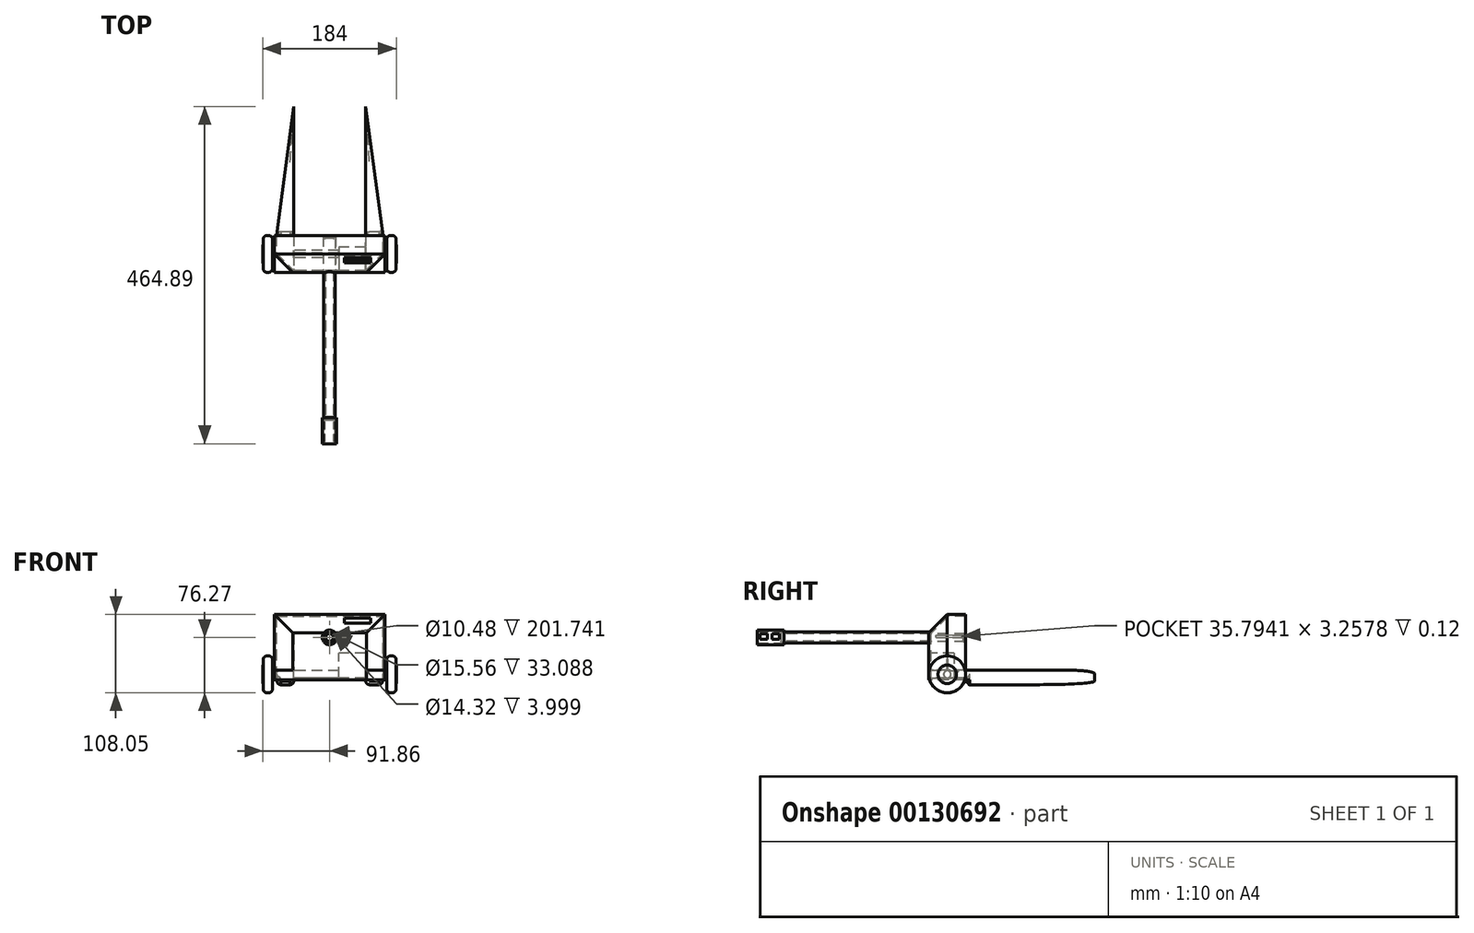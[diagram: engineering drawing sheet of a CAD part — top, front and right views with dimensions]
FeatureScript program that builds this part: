
annotation { "Feature Type Name" : "Feature", "Feature Type Description" : "" }
export const myFeature = defineFeature(function(context is Context, id is Id, definition is map)
    precondition{}
    {
        {
            var Q0;
            Q0=qCreatedBy(makeId("Front.planeOp"),FACE);
            var sketch = newSketch(context, id + "F0", { "sketchPlane" : qUnion([Q0])});
            skCircle(sketch, "E0", {"center": v(0, 0) * mm, "radius": 7.78 * mm});
            skCircle(sketch, "E1", {"center": v(0, 0) * mm, "radius": 10.04 * mm});
            skSolve(sketch);
        }
        {
            var Q0;
            Q0=makeQuery(id+"F0.imprint","IMPRINT",FACE,{"disambiguationData":[TD([[makeQuery(id+"F0.imprint","IMPRINT",EDGE,{"derivedFrom":sQuery(id+"F0.wireOp",EDGE,"E0")}),-1.0]])]});
            extrude(context, id + "F1", {"entities" : qUnion([Q0]), "depth" : 33.1 * mm, "hasSecondDirection" : true, "secondDirectionOppositeDirection" : true, "secondDirectionDepth" : 3.3 * mm});
        }
        {
            var Q0;
            Q0=makeQuery(id+"F0.imprint","IMPRINT",FACE,{"disambiguationData":[TD([[makeQuery(id+"F0.imprint","IMPRINT",EDGE,{"derivedFrom":sQuery(id+"F0.wireOp",EDGE,"E0")}),1.0]])]});
            extrude(context, id + "F2", {"entities" : qUnion([Q0]), "operationType" : NewBodyOperationType.ADD, "oppositeDirection" : true, "depth" : 203.2 * mm});
        }
        {
            var Q0;
            Q0=makeQuery(id+"F2.opExtrude","CAP_FACE",FACE,{"disambiguationData":[OSD([sQuery(id+"F0.wireOp",EDGE,"E0")])],"isStart":false});
            var sketch = newSketch(context, id + "F3", { "sketchPlane" : qUnion([Q0])});
            skLineSegment(sketch, "E2.bottom", {"start": v(-76.37, 31.78) * mm, "end": v(76.03, 31.78) * mm});
            skLineSegment(sketch, "E2.top", {"start": v(-76.37, -58.3) * mm, "end": v(76.03, -58.3) * mm});
            skLineSegment(sketch, "E2.left", {"start": v(-76.37, 31.78) * mm, "end": v(-76.37, -58.3) * mm});
            skLineSegment(sketch, "E2.right", {"start": v(76.03, 31.78) * mm, "end": v(76.03, -58.3) * mm});
            skSolve(sketch);
        }
        {
            var Q0;
            Q0 = qSketchRegion(id + "F3", true);
            extrude(context, id + "F4", {"entities" : qUnion([Q0]), "operationType" : NewBodyOperationType.ADD, "depth" : 50.8 * mm});
        }
        {
            var Q0;
            Q0=makeQuery(id+"F4.opExtrude","CAP_EDGE",EDGE,{"disambiguationData":[OSD([sQuery(id+"F3.wireOp",EDGE,"E2.right")])],"isStart":true});
            var Q1;
            Q1=makeQuery(id+"F4.opExtrude","CAP_EDGE",EDGE,{"disambiguationData":[OSD([sQuery(id+"F3.wireOp",EDGE,"E2.left")])],"isStart":true});
            var Q2;
            Q2=makeQuery(id+"F4.opExtrude","CAP_EDGE",EDGE,{"disambiguationData":[OSD([sQuery(id+"F3.wireOp",EDGE,"E2.bottom")])],"isStart":true});
            chamfer(context, id + "F5", {"entities" : qUnion([Q0, Q1, Q2]), "width" : 25.4 * mm, "tangentPropagation" : true});
        }
        {
            var Q0;
            Q0=makeQuery(id+"F4.opExtrude","CAP_FACE",FACE,{"disambiguationData":[OSD([sQuery(id+"F3.wireOp",EDGE,"E2.bottom"),sQuery(id+"F3.wireOp",EDGE,"E2.top"),sQuery(id+"F3.wireOp",EDGE,"E2.left"),sQuery(id+"F3.wireOp",EDGE,"E2.right")])],"isStart":false});
            shell(context, id + "F6", {"entities" : qUnion([Q0]), "thickness" : 2.54 * mm});
        }
        {
            var Q0;
            Q0=qCreatedBy(makeId("Front.planeOp"),FACE);
            var sketch = newSketch(context, id + "F7", { "sketchPlane" : qUnion([Q0])});
            skLineSegment(sketch, "E3.bottom", {"start": v(20.34, 26.67) * mm, "end": v(56.85, 26.67) * mm});
            skLineSegment(sketch, "E3.top", {"start": v(20.34, 19.54) * mm, "end": v(56.85, 19.54) * mm});
            skLineSegment(sketch, "E3.left", {"start": v(20.34, 26.67) * mm, "end": v(20.34, 19.54) * mm});
            skLineSegment(sketch, "E3.right", {"start": v(56.85, 26.67) * mm, "end": v(56.85, 19.54) * mm});
            skSolve(sketch);
        }
        {
            var Q0;
            Q0 = qSketchRegion(id + "F7", true);
            extrude(context, id + "F8", {"entities" : qUnion([Q0]), "operationType" : NewBodyOperationType.REMOVE, "oppositeDirection" : true, "depth" : 279.63 * mm});
        }
        {
            var Q0;
            Q0=qCreatedBy(makeId("Right.planeOp"),FACE);
            var sketch = newSketch(context, id + "F9", { "sketchPlane" : qUnion([Q0])});
            skLineSegment(sketch, "E4.bottom", {"start": v(-29.7, 5.03) * mm, "end": v(-19.53, 5.03) * mm});
            skLineSegment(sketch, "E4.top", {"start": v(-29.7, -2.59) * mm, "end": v(-19.53, -2.59) * mm});
            skLineSegment(sketch, "E4.left", {"start": v(-29.7, 5.03) * mm, "end": v(-29.7, -2.59) * mm});
            skLineSegment(sketch, "E4.right", {"start": v(-19.53, 5.03) * mm, "end": v(-19.53, -2.59) * mm});
            skLineSegment(sketch, "E5.bottom", {"start": v(-12.8, 5.03) * mm, "end": v(-2.65, 5.03) * mm});
            skLineSegment(sketch, "E5.top", {"start": v(-12.8, -2.59) * mm, "end": v(-2.65, -2.59) * mm});
            skLineSegment(sketch, "E5.left", {"start": v(-12.8, 5.03) * mm, "end": v(-12.8, -2.59) * mm});
            skLineSegment(sketch, "E5.right", {"start": v(-2.65, 5.03) * mm, "end": v(-2.65, -2.59) * mm});
            skSolve(sketch);
        }
        {
            var Q0;
            Q0 = qSketchRegion(id + "F9", true);
            extrude(context, id + "F10", {"entities" : qUnion([Q0]), "operationType" : NewBodyOperationType.REMOVE, "oppositeDirection" : true, "depth" : 25.4 * mm, "hasSecondDirection" : true, "secondDirectionOppositeDirection" : false, "secondDirectionDepth" : 29.94 * mm});
        }
        {
            var Q0;
            Q0=makeQuery(id+"F0.imprint","IMPRINT",FACE,{"disambiguationData":[TD([[makeQuery(id+"F0.imprint","IMPRINT",EDGE,{"derivedFrom":sQuery(id+"F0.wireOp",EDGE,"E0")}),1.0]])]});
            var sketch = newSketch(context, id + "F11", { "sketchPlane" : qUnion([Q0])});
            skCircle(sketch, "E6", {"center": v(0, 0) * mm, "radius": 7.16 * mm});
            skSolve(sketch);
        }
        {
            var Q0;
            Q0 = qSketchRegion(id + "F11", true);
            extrude(context, id + "F12", {"entities" : qUnion([Q0]), "operationType" : NewBodyOperationType.REMOVE, "oppositeDirection" : true, "depth" : 4 * mm});
        }
        {
            var Q0;
            Q0=makeQuery(id+"F4.opExtrude","SWEPT_FACE",FACE,{"disambiguationData":[OSD([sQuery(id+"F3.wireOp",EDGE,"E2.left")])]});
            var sketch = newSketch(context, id + "F13", { "sketchPlane" : qUnion([Q0])});
            skLineSegment(sketch, "E7.bottom", {"start": v(254, -58.3) * mm, "end": v(203.24, -58.3) * mm});
            skLineSegment(sketch, "E7.top", {"start": v(254, -45) * mm, "end": v(203.24, -45) * mm});
            skLineSegment(sketch, "E7.left", {"start": v(254, -58.3) * mm, "end": v(254, -45) * mm});
            skLineSegment(sketch, "E7.right", {"start": v(203.24, -58.3) * mm, "end": v(203.24, -45) * mm});
            skSolve(sketch);
        }
        {
            var Q0;
            Q0 = qSketchRegion(id + "F13", true);
            extrude(context, id + "F14", {"entities" : qUnion([Q0]), "operationType" : NewBodyOperationType.ADD, "oppositeDirection" : true, "depth" : 26.42 * mm});
        }
        {
            var Q0;
            Q0=makeQuery(id+"F4.opExtrude","SWEPT_FACE",FACE,{"disambiguationData":[OSD([sQuery(id+"F3.wireOp",EDGE,"E2.right")])]});
            var sketch = newSketch(context, id + "F15", { "sketchPlane" : qUnion([Q0])});
            skLineSegment(sketch, "E8.bottom", {"start": v(-254, -58.3) * mm, "end": v(-203.2, -58.3) * mm});
            skLineSegment(sketch, "E8.top", {"start": v(-254, -45) * mm, "end": v(-203.2, -45) * mm});
            skLineSegment(sketch, "E8.left", {"start": v(-254, -58.3) * mm, "end": v(-254, -45) * mm});
            skLineSegment(sketch, "E8.right", {"start": v(-203.2, -58.3) * mm, "end": v(-203.2, -45) * mm});
            skSolve(sketch);
        }
        {
            var Q0;
            Q0 = qSketchRegion(id + "F15", true);
            extrude(context, id + "F16", {"entities" : qUnion([Q0]), "operationType" : NewBodyOperationType.ADD, "oppositeDirection" : true, "depth" : 26.47 * mm});
        }
        {
            var Q0;
            Q0=makeQuery(id+"F6.opShell","OFFSET_FACE",FACE,{"disambiguationData":[OSD([sQuery(id+"F3.wireOp",EDGE,"E2.bottom"),sQuery(id+"F3.wireOp",EDGE,"E2.top"),sQuery(id+"F3.wireOp",EDGE,"E2.left"),sQuery(id+"F3.wireOp",EDGE,"E2.right")])]});
            var sketch = newSketch(context, id + "F17", { "sketchPlane" : qUnion([Q0])});
            skLineSegment(sketch, "E9.bottom", {"start": v(-8.58, 5.33) * mm, "end": v(8.55, 5.33) * mm});
            skLineSegment(sketch, "E9.top", {"start": v(-8.58, -5.4) * mm, "end": v(8.55, -5.4) * mm});
            skLineSegment(sketch, "E9.left", {"start": v(-8.58, 5.33) * mm, "end": v(-8.58, -5.4) * mm});
            skLineSegment(sketch, "E9.right", {"start": v(8.55, 5.33) * mm, "end": v(8.55, -5.4) * mm});
            skSolve(sketch);
        }
        {
            var Q0;
            Q0 = qSketchRegion(id + "F17", true);
            extrude(context, id + "F18", {"entities" : qUnion([Q0]), "operationType" : NewBodyOperationType.ADD, "depth" : 47.6 * mm});
        }
        {
            var Q0;
            Q0=makeQuery(id+"F18.opExtrude","SWEPT_FACE",FACE,{"disambiguationData":[OSD([sQuery(id+"F17.wireOp",EDGE,"E9.left")])]});
            var sketch = newSketch(context, id + "F19", { "sketchPlane" : qUnion([Q0])});
            skLineSegment(sketch, "E10.bottom", {"start": v(213.2, 0) * mm, "end": v(249, 0) * mm});
            skLineSegment(sketch, "E10.top", {"start": v(213.2, 3.26) * mm, "end": v(249, 3.26) * mm});
            skLineSegment(sketch, "E10.left", {"start": v(213.2, 0) * mm, "end": v(213.2, 3.26) * mm});
            skLineSegment(sketch, "E10.right", {"start": v(249, 0) * mm, "end": v(249, 3.26) * mm});
            skSolve(sketch);
        }
        {
            var Q0;
            Q0=makeQuery(id+"F19.imprint","IMPRINT",FACE,{"disambiguationData":[TD([[makeQuery(id+"F19.imprint","IMPRINT",EDGE,{"derivedFrom":sQuery(id+"F19.wireOp",EDGE,"E10.bottom")}),1.0]])]});
            extrude(context, id + "F20", {"entities" : qUnion([Q0]), "operationType" : NewBodyOperationType.REMOVE, "oppositeDirection" : true, "depth" : 0.12 * mm});
        }
        {
            var Q0;
            Q0=makeQuery(id+"F18.opExtrude","CAP_FACE",FACE,{"disambiguationData":[OSD([sQuery(id+"F17.wireOp",EDGE,"E9.bottom"),sQuery(id+"F17.wireOp",EDGE,"E9.top"),sQuery(id+"F17.wireOp",EDGE,"E9.left"),sQuery(id+"F17.wireOp",EDGE,"E9.right")])],"isStart":false});
            var sketch = newSketch(context, id + "F21", { "sketchPlane" : qUnion([Q0])});
            skArc(sketch, "E11", {"start": v(-5.15, 5.33) * mm, "mid": v(0.25, -5.46) * mm, "end": v(5.65, 5.33) * mm});
            skSolve(sketch);
        }
        {
            var Q0;
            Q0 = qSketchRegion(id + "F21", true);
            var Q1;
            {var subQ0=sQuery(id+"F21.wireOp",EDGE,"E11");var subQ1=makeQuery(id+"F18.opExtrude","CAP_EDGE",EDGE,{"disambiguationData":[OSD([sQuery(id+"F17.wireOp",EDGE,"E9.bottom")])],"isStart":false});var subQ2=makeQuery(id+"F21.imprint","INTERSECT",VERTEX,{"disambiguationData":[OD(0.0)],"derivedFrom":[subQ1,subQ0]});Q1=makeQuery(id+"F21.imprint","IMPRINT",FACE,{"disambiguationData":[TD([[makeQuery(id+"F21.imprint","IMPRINT",EDGE,{"disambiguationData":[TD([[subQ2,-1.0]])],"derivedFrom":subQ0}),1.0]])]});}
            extrude(context, id + "F22", {"entities" : qUnion([Q0, Q1]), "operationType" : NewBodyOperationType.REMOVE, "oppositeDirection" : true, "depth" : 3 * mm});
        }
        {
            var Q0;
            Q0=makeQuery(id+"F6.opShell","OFFSET_FACE",FACE,{"disambiguationData":[OSD([sQuery(id+"F3.wireOp",EDGE,"E2.bottom"),sQuery(id+"F3.wireOp",EDGE,"E2.top"),sQuery(id+"F3.wireOp",EDGE,"E2.left"),sQuery(id+"F3.wireOp",EDGE,"E2.right")])]});
            var sketch = newSketch(context, id + "F23", { "sketchPlane" : qUnion([Q0])});
            skLineSegment(sketch, "E12.bottom", {"start": v(-49.92, -55.77) * mm, "end": v(-13.15, -55.77) * mm});
            skLineSegment(sketch, "E12.top", {"start": v(-49.92, -21.29) * mm, "end": v(-13.15, -21.29) * mm});
            skLineSegment(sketch, "E12.left", {"start": v(-49.92, -55.77) * mm, "end": v(-49.92, -21.29) * mm});
            skLineSegment(sketch, "E12.right", {"start": v(-13.15, -55.77) * mm, "end": v(-13.15, -21.29) * mm});
            skSolve(sketch);
        }
        {
            var Q0;
            Q0 = qSketchRegion(id + "F23", true);
            extrude(context, id + "F24", {"entities" : qUnion([Q0]), "operationType" : NewBodyOperationType.ADD, "depth" : 32.25 * mm});
        }
        {
            var Q0;
            Q0=makeQuery(id+"F14.boolean.opBoolean","MERGE",FACE,{"derivedFrom":[makeQuery(id+"F4.opExtrude","SWEPT_FACE",FACE,{"disambiguationData":[OSD([sQuery(id+"F3.wireOp",EDGE,"E2.left")])]}),makeQuery(id+"F14.opExtrude","CAP_FACE",FACE,{"disambiguationData":[OSD([sQuery(id+"F13.wireOp",EDGE,"E7.bottom"),sQuery(id+"F13.wireOp",EDGE,"E7.top"),sQuery(id+"F13.wireOp",EDGE,"E7.left"),sQuery(id+"F13.wireOp",EDGE,"E7.right")])],"isStart":true})]});
            var sketch = newSketch(context, id + "F25", { "sketchPlane" : qUnion([Q0])});
            skCircle(sketch, "E13", {"center": v(228.6, -50.87) * mm, "radius": 4.97 * mm});
            skSolve(sketch);
        }
        {
            var Q0;
            Q0 = qSketchRegion(id + "F25", true);
            extrude(context, id + "F26", {"entities" : qUnion([Q0]), "operationType" : NewBodyOperationType.ADD, "depth" : 2.56 * mm, "hasSecondDirection" : true, "secondDirectionOppositeDirection" : true, "secondDirectionDepth" : 155.02 * mm});
        }
        {
            var Q0;
            Q0=makeQuery(id+"F26.opExtrude","CAP_FACE",FACE,{"disambiguationData":[OSD([sQuery(id+"F25.wireOp",EDGE,"E13")])],"isStart":false});
            var sketch = newSketch(context, id + "F27", { "sketchPlane" : qUnion([Q0])});
            skCircle(sketch, "E14", {"center": v(228.6, -50.87) * mm, "radius": 25.4 * mm});
            skSolve(sketch);
        }
        {
            var Q0;
            Q0 = qSketchRegion(id + "F27", true);
            extrude(context, id + "F28", {"entities" : qUnion([Q0]), "depth" : 12.7 * mm});
        }
        {
            var Q0;
            Q0=makeQuery(id+"F26.opExtrude","CAP_FACE",FACE,{"disambiguationData":[OSD([sQuery(id+"F25.wireOp",EDGE,"E13")])],"isStart":true});
            var sketch = newSketch(context, id + "F29", { "sketchPlane" : qUnion([Q0])});
            skCircle(sketch, "E15", {"center": v(-228.6, -50.87) * mm, "radius": 25.4 * mm});
            skSolve(sketch);
        }
        {
            var Q0;
            Q0 = qSketchRegion(id + "F29", true);
            extrude(context, id + "F30", {"entities" : qUnion([Q0]), "depth" : 12.7 * mm});
        }
        {
            var Q0;
            {var subQ0=sQuery(id+"F13.wireOp",EDGE,"E7.left");var subQ1=sQuery(id+"F13.wireOp",EDGE,"E7.top");Q0=makeQuery(id+"F14.boolean.opBoolean","SPLIT",FACE,{"disambiguationData":[TD([makeQuery(id+"F14.opExtrude","SWEPT_FACE",FACE,{"disambiguationData":[OSD([subQ0])]})])],"derivedFrom":makeQuery(id+"F14.opExtrude","SWEPT_FACE",FACE,{"disambiguationData":[OSD([subQ1])]})});}
            var sketch = newSketch(context, id + "F31", { "sketchPlane" : qUnion([Q0])});
            skLineSegment(sketch, "E16", {"start": v(49.95, 254) * mm, "end": v(49.95, 431.8) * mm});
            skLineSegment(sketch, "E17", {"start": v(49.95, 431.8) * mm, "end": v(73.83, 254) * mm});
            skLineSegment(sketch, "E18", {"start": v(73.83, 254) * mm, "end": v(49.95, 254) * mm});
            skLineSegment(sketch, "E19", {"start": v(-49.35, 254) * mm, "end": v(-49.35, 431.8) * mm});
            skLineSegment(sketch, "E20", {"start": v(-49.35, 431.8) * mm, "end": v(-73.05, 253.55) * mm});
            skLineSegment(sketch, "E21", {"start": v(-73.05, 253.55) * mm, "end": v(-49.35, 254) * mm});
            skSolve(sketch);
        }
        {
            var Q0;
            Q0 = qSketchRegion(id + "F31", true);
            extrude(context, id + "F32", {"entities" : qUnion([Q0]), "operationType" : NewBodyOperationType.ADD, "oppositeDirection" : true, "depth" : 20.12 * mm});
        }
        {
            var Q0;
            Q0=makeQuery(id+"F32.opExtrude","CAP_EDGE",EDGE,{"disambiguationData":[OSD([sQuery(id+"F31.wireOp",EDGE,"E17")])],"isStart":true});
            var Q1;
            Q1=makeQuery(id+"F32.opExtrude","CAP_EDGE",EDGE,{"disambiguationData":[OSD([sQuery(id+"F31.wireOp",EDGE,"E17")])],"isStart":false});
            var Q2;
            Q2=makeQuery(id+"F32.opExtrude","CAP_EDGE",EDGE,{"disambiguationData":[OSD([sQuery(id+"F31.wireOp",EDGE,"E16")])],"isStart":false});
            fillet(context, id + "F33", {"entities" : qUnion([Q0, Q1, Q2]), "radius" : 5.08 * mm, "tangentPropagation" : true, "allowEdgeOverflow" : false});
        }
        {
            var Q0;
            Q0=makeQuery(id+"F32.opExtrude","CAP_EDGE",EDGE,{"disambiguationData":[OSD([sQuery(id+"F31.wireOp",EDGE,"E20")])],"isStart":true});
            var Q1;
            Q1=makeQuery(id+"F32.opExtrude","CAP_EDGE",EDGE,{"disambiguationData":[OSD([sQuery(id+"F31.wireOp",EDGE,"E19")])],"isStart":false});
            var Q2;
            Q2=makeQuery(id+"F32.opExtrude","CAP_EDGE",EDGE,{"disambiguationData":[OSD([sQuery(id+"F31.wireOp",EDGE,"E20")])],"isStart":false});
            fillet(context, id + "F34", {"entities" : qUnion([Q0, Q1, Q2]), "radius" : 5.08 * mm, "tangentPropagation" : true, "allowEdgeOverflow" : false});
        }
        {
            var Q0;
            Q0=makeQuery(id+"F28.opExtrude","CAP_EDGE",EDGE,{"disambiguationData":[OSD([sQuery(id+"F27.wireOp",EDGE,"E14")])],"isStart":false});
            var Q1;
            Q1=makeQuery(id+"F30.opExtrude","CAP_EDGE",EDGE,{"disambiguationData":[OSD([sQuery(id+"F29.wireOp",EDGE,"E15")])],"isStart":false});
            var Q2;
            Q2=makeQuery(id+"F30.opExtrude","CAP_EDGE",EDGE,{"disambiguationData":[OSD([sQuery(id+"F29.wireOp",EDGE,"E15")])],"isStart":true});
            var Q3;
            Q3=makeQuery(id+"F28.opExtrude","CAP_EDGE",EDGE,{"disambiguationData":[OSD([sQuery(id+"F27.wireOp",EDGE,"E14")])],"isStart":true});
            fillet(context, id + "F35", {"entities" : qUnion([Q0, Q1, Q2, Q3]), "radius" : 5.08 * mm, "tangentPropagation" : true, "allowEdgeOverflow" : false});
        }
        {
            var Q0;
            Q0=makeQuery(id+"F28.opExtrude","CAP_FACE",FACE,{"disambiguationData":[OSD([sQuery(id+"F27.wireOp",EDGE,"E14")])],"isStart":false});
            var sketch = newSketch(context, id + "F36", { "sketchPlane" : qUnion([Q0])});
            skCircle(sketch, "E22", {"center": v(228.6, -50.87) * mm, "radius": 12.7 * mm});
            skSolve(sketch);
        }
        {
            var Q0;
            Q0=makeQuery(id+"F36.imprint","IMPRINT",FACE,{"disambiguationData":[TD([[makeQuery(id+"F36.imprint","IMPRINT",EDGE,{"derivedFrom":sQuery(id+"F36.wireOp",EDGE,"E22")}),1.0]])]});
            extrude(context, id + "F37", {"entities" : qUnion([Q0]), "depth" : 0.5 * mm});
        }
        {
            var Q0;
            Q0=makeQuery(id+"F30.opExtrude","CAP_FACE",FACE,{"disambiguationData":[OSD([sQuery(id+"F29.wireOp",EDGE,"E15")])],"isStart":false});
            var sketch = newSketch(context, id + "F38", { "sketchPlane" : qUnion([Q0])});
            skCircle(sketch, "E23", {"center": v(-228.6, -50.87) * mm, "radius": 12.7 * mm});
            skSolve(sketch);
        }
        {
            var Q0;
            Q0 = qSketchRegion(id + "F38", true);
            extrude(context, id + "F39", {"entities" : qUnion([Q0]), "depth" : 0.5 * mm});
        }
        {
            var Q0;
            Q0=makeQuery(id+"F32.opExtrude","CAP_EDGE",EDGE,{"disambiguationData":[OSD([sQuery(id+"F31.wireOp",EDGE,"E21")])],"isStart":false});
            var Q1;
            Q1=makeQuery(id+"F32.opExtrude","CAP_EDGE",EDGE,{"disambiguationData":[OSD([sQuery(id+"F31.wireOp",EDGE,"E18")])],"isStart":false});
            chamfer(context, id + "F40", {"entities" : qUnion([Q0, Q1]), "width" : 5.08 * mm, "tangentPropagation" : true});
        }
    });
